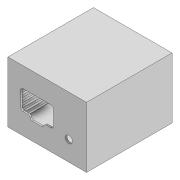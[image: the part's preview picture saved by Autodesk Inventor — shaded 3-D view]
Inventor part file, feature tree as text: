
AUTODESK INVENTOR PART (.ipt)
format: ipt  version: 2020 (Build 240168000, 168)  size: 304,640 bytes
history: native  units: in
note: dims shown in document units (in); Inventor stores cm internally (conversion verified against a paired STEP export)
features: extrude x3, sketch x3, fillet x2, hole x1
ambient origin geometry x8: Origin, YZ Plane, XZ Plane, XY Plane, X Axis, Y Axis, Z Axis, Center Point
bodies: Solid1 (feature_tree)
feature tree (9):
  extrude  "Extrusion1"  Depth=2.0472in
  extrude  "Extrusion2"  Depth=2.8346in
  fillet  "Fillet2"  Radius=2.8346in
  extrude  "Extrusion3"  Depth=0.0709in
  hole  "Hole1"  [1 undecoded]
  fillet  "Fillet4"  Radius=0.1496in
  sketch  "Sketch1"  dims[d0=2.65in d1=2.0472in]
  sketch  "Sketch2"  dims[d2=2.54in d3=1.9055in d27=2.8346in d28=0.0in]
  sketch  "Sketch4"  dims[d32=0.15in d33=0.0709in d34=0.1in d35=3.1496in d37=0.1496in d38=0.3937in d40=1.0in d42=0.2362in d44=0.05in d45=0.0in d46=0.6693in d47=0.5906in d48=1.1024in d49=0.7874in d50=0.5906in d51=0.4331in d52=0.0787in d54=2.65in d55=2.0472in d56=2.54in d57=1.9055in d58=0.315in d59=0.315in d60=0.315in d61=0.315in d62=0.315in d63=0.315in d64=0.315in d65=0.315in d66=0.1575in d67=0.0in d69=0.1575in d70=0.1575in d71=0.1575in d72=0.1575in d73=0.1535in d74=0.315in d75=0.1575in d76=0.0787in d77=90.0deg d78=0.4646in d79=0.8108in d81=0.315in d82=0.1181in d83=0.315in d84=0.1181in d85=0.0787in]
note: 1 required parameter value undecoded (feature->parameter linkage not recoverable at this tier; creation-order binding heuristic only, values carry confidence <= 0.55)
